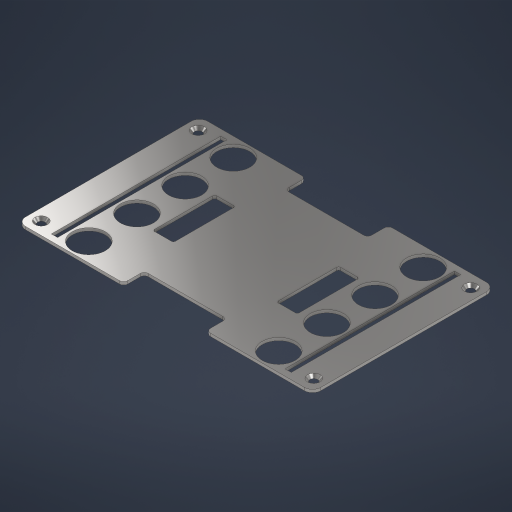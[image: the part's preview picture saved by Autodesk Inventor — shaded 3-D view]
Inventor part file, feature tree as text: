
AUTODESK INVENTOR PART (.ipt)
format: ipt  version: 2024 (Build 280153000, 153)  size: 403,456 bytes
history: native  units: in
note: dims shown in document units (in); Inventor stores cm internally (conversion verified against a paired STEP export)
features: extrude x4, sketch x3, hole x2, fillet x1
ambient origin geometry x8: Origin, YZ Plane, XZ Plane, XY Plane, X Axis, Y Axis, Z Axis, Center Point
bodies: Solid1 (feature_tree)
feature tree (10):
  extrude  "Extrusion1"  Depth=2.815in
  hole  "Hole1"  [1 undecoded]
  extrude  "Extrusion2"  TaperAngle=0.0deg  [1 undecoded]
  hole  "Hole4"  [1 undecoded]
  fillet  "Fillet3"  Radius=1.1811in
  extrude  "Extrusion6"  Depth=0.5906in
  extrude  "Extrusion7"  Depth=1.6142in
  sketch  "Sketch8"  dims[d0=1.7362in d1=2.815in]
  sketch  "Sketch9"  dims[d3=0.0276in d4=0.0in]
  sketch  "Sketch10"  dims[d9=0.07in d10=0.146in d11=0.119in d12=0.25in d13=0.5635in d14=1.0in d15=0.8108in d18=0.5906in d19=0.0in d20=0.0in d21=0.1969in d72=1.1811in d73=0.5906in d77=1.4961in d78=0.748in d79=1.2992in d85=0.0197in d88=0.0197in d89=0.0197in d90=0.0197in d91=0.1969in d92=0.5906in d101=0.2297in d102=0.2297in d103=0.4593in d104=0.4593in d105=0.315in d106=0.38in d107=0.4in d108=0.61in d109=90.0deg d110=0.315in d111=0.8108in d113=0.9055in d114=0.0787in d115=1.2992in d116=0.1969in d117=0.7874in d118=0.3937in d119=0.0394in d120=0.0394in d121=0.0394in d122=0.0in d123=0.0in d124=0.0591in d125=1.6142in d126=1.0846in d127=0.0in d128=0.0in]
note: 3 required parameter values undecoded (feature->parameter linkage not recoverable at this tier; creation-order binding heuristic only, values carry confidence <= 0.55)
